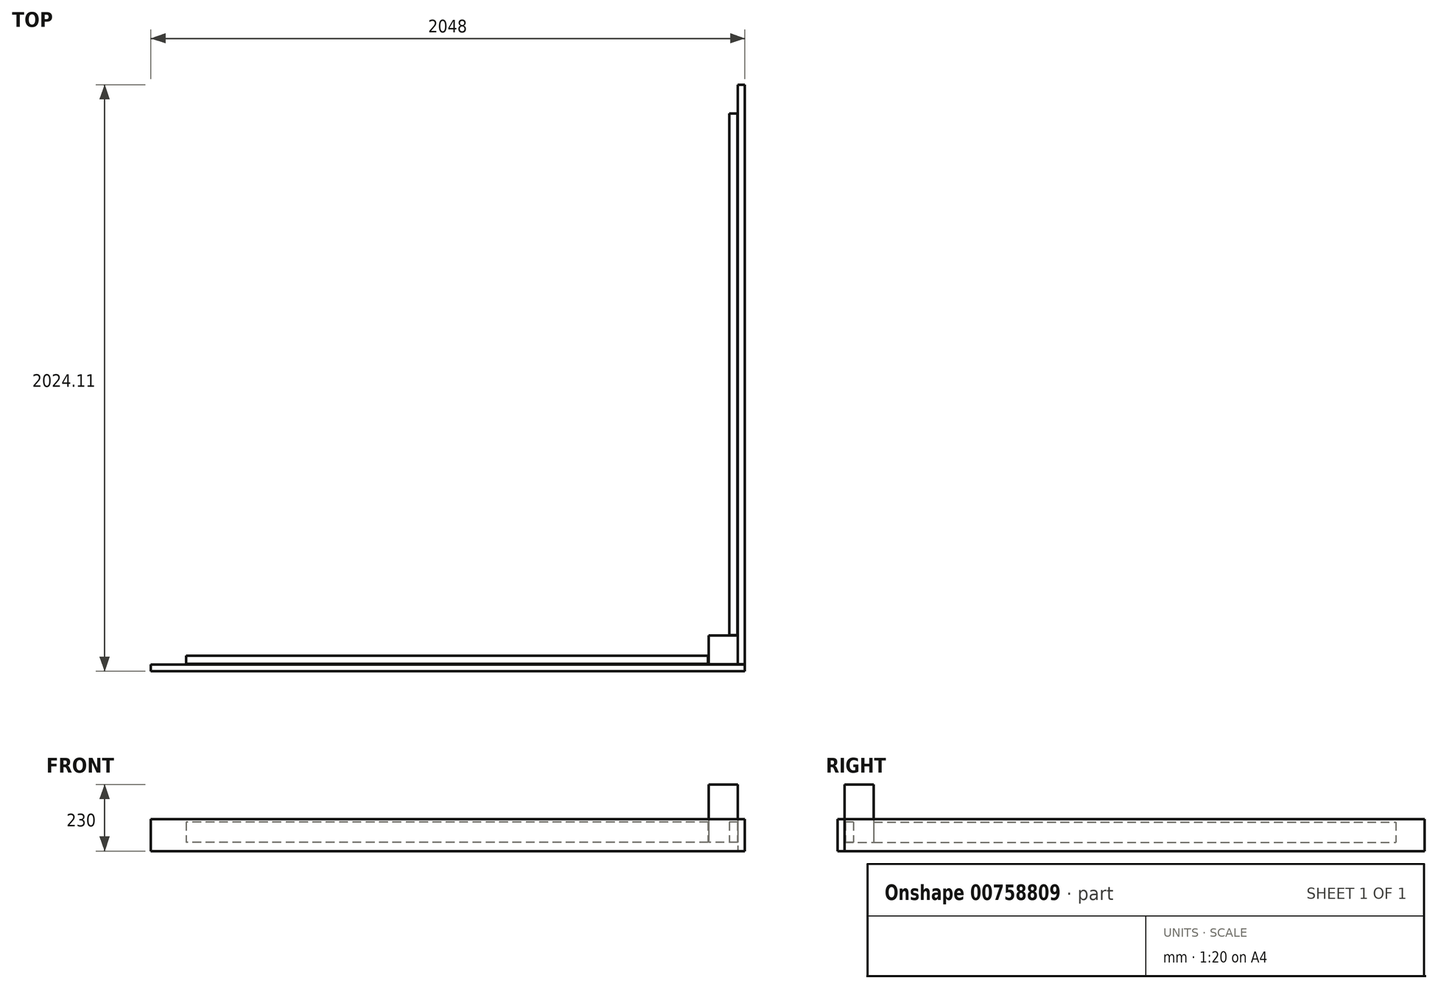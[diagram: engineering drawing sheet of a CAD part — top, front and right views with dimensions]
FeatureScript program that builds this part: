
annotation { "Feature Type Name" : "Feature", "Feature Type Description" : "" }
export const myFeature = defineFeature(function(context is Context, id is Id, definition is map)
    precondition{}
    {
        {
            var Q0;
            Q0=qCreatedBy(makeId("Top.planeOp"),FACE);
            var sketch = newSketch(context, id + "F0", { "sketchPlane" : qUnion([Q0])});
            skLineSegment(sketch, "E0.bottom", {"start": v(50, -50) * mm, "end": v(-50, -50) * mm});
            skLineSegment(sketch, "E0.top", {"start": v(50, 50) * mm, "end": v(-50, 50) * mm});
            skLineSegment(sketch, "E0.left", {"start": v(50, -50) * mm, "end": v(50, 50) * mm});
            skLineSegment(sketch, "E0.right", {"start": v(-50, -50) * mm, "end": v(-50, 50) * mm});
            skPoint(sketch, "E0.middle", {"position": v(0, 0) * mm});
            skSolve(sketch);
        }
        {
            var Q0;
            Q0 = qSketchRegion(id + "F0", true);
            extrude(context, id + "F1", {"entities" : qUnion([Q0]), "depth" : 200 * mm, "offsetDistance" : 25 * mm});
        }
        {
            var Q0;
            Q0=qCreatedBy(makeId("Top.planeOp"),FACE);
            var sketch = newSketch(context, id + "F2", { "sketchPlane" : qUnion([Q0])});
            skLineSegment(sketch, "E1.bottom", {"start": v(50.75, 1949.98) * mm, "end": v(74.75, 1949.98) * mm});
            skLineSegment(sketch, "E1.top", {"start": v(50.75, -50.02) * mm, "end": v(74.75, -50.02) * mm});
            skLineSegment(sketch, "E1.left", {"start": v(50.75, 1949.98) * mm, "end": v(50.75, -50.02) * mm});
            skLineSegment(sketch, "E1.right", {"start": v(74.75, 1949.98) * mm, "end": v(74.75, -50.02) * mm});
            skSolve(sketch);
        }
        {
            var Q0;
            Q0 = qSketchRegion(id + "F2", true);
            extrude(context, id + "F3", {"entities" : qUnion([Q0]), "depth" : 110 * mm, "offsetDistance" : 25 * mm});
        }
        {
            var Q0;
            Q0=makeQuery(id+"F3.opExtrude","SWEPT_BODY",BODY,{"disambiguationData":[OSD([sQuery(id+"F2.wireOp",EDGE,"E1.bottom"),sQuery(id+"F2.wireOp",EDGE,"E1.top"),sQuery(id+"F2.wireOp",EDGE,"E1.left"),sQuery(id+"F2.wireOp",EDGE,"E1.right")])]});
            transform(context, id + "F4", {"entities" : qUnion([Q0]), "transformType" : TransformType.TRANSLATION_3D, "dx" : 0 * mm, "dy" : 0 * mm, "dz" : -30 * mm, "makeCopy" : false});
        }
        {
            var Q0;
            Q0=qCreatedBy(makeId("Top.planeOp"),FACE);
            var sketch = newSketch(context, id + "F5", { "sketchPlane" : qUnion([Q0])});
            skLineSegment(sketch, "E2.bottom", {"start": v(49.68, 50.74) * mm, "end": v(21.68, 50.74) * mm});
            skLineSegment(sketch, "E2.top", {"start": v(49.68, 1850.74) * mm, "end": v(21.68, 1850.74) * mm});
            skLineSegment(sketch, "E2.left", {"start": v(49.68, 50.74) * mm, "end": v(49.68, 1850.74) * mm});
            skLineSegment(sketch, "E2.right", {"start": v(21.68, 50.74) * mm, "end": v(21.68, 1850.74) * mm});
            skSolve(sketch);
        }
        {
            var Q0;
            Q0 = qSketchRegion(id + "F5", true);
            extrude(context, id + "F6", {"entities" : qUnion([Q0]), "depth" : 70 * mm, "offsetDistance" : 25 * mm});
        }
        {
            var Q0;
            Q0=qCreatedBy(makeId("Top.planeOp"),FACE);
            var sketch = newSketch(context, id + "F7", { "sketchPlane" : qUnion([Q0])});
            skLineSegment(sketch, "E3.bottom", {"start": v(74.76, -50.13) * mm, "end": v(-1973.24, -50.13) * mm});
            skLineSegment(sketch, "E3.top", {"start": v(74.76, -74.13) * mm, "end": v(-1973.24, -74.13) * mm});
            skLineSegment(sketch, "E3.left", {"start": v(74.76, -50.13) * mm, "end": v(74.76, -74.13) * mm});
            skLineSegment(sketch, "E3.right", {"start": v(-1973.24, -50.13) * mm, "end": v(-1973.24, -74.13) * mm});
            skSolve(sketch);
        }
        {
            var Q0;
            Q0 = qSketchRegion(id + "F7", true);
            extrude(context, id + "F8", {"entities" : qUnion([Q0]), "depth" : 110 * mm, "offsetDistance" : 25 * mm});
        }
        {
            var Q0;
            Q0=makeQuery(id+"F8.opExtrude","SWEPT_BODY",BODY,{"disambiguationData":[OSD([sQuery(id+"F7.wireOp",EDGE,"E3.bottom"),sQuery(id+"F7.wireOp",EDGE,"E3.top"),sQuery(id+"F7.wireOp",EDGE,"E3.left"),sQuery(id+"F7.wireOp",EDGE,"E3.right")])]});
            transform(context, id + "F9", {"entities" : qUnion([Q0]), "transformType" : TransformType.TRANSLATION_3D, "dx" : 0 * mm, "dy" : 0 * mm, "dz" : -30 * mm, "makeCopy" : false});
        }
        {
            var Q0;
            Q0=qCreatedBy(makeId("Top.planeOp"),FACE);
            var sketch = newSketch(context, id + "F10", { "sketchPlane" : qUnion([Q0])});
            skLineSegment(sketch, "E4.bottom", {"start": v(-52.17, -19.74) * mm, "end": v(-1852.17, -19.74) * mm});
            skLineSegment(sketch, "E4.top", {"start": v(-52.17, -47.74) * mm, "end": v(-1852.17, -47.74) * mm});
            skLineSegment(sketch, "E4.left", {"start": v(-52.17, -19.74) * mm, "end": v(-52.17, -47.74) * mm});
            skLineSegment(sketch, "E4.right", {"start": v(-1852.17, -19.74) * mm, "end": v(-1852.17, -47.74) * mm});
            skSolve(sketch);
        }
        {
            var Q0;
            Q0 = qSketchRegion(id + "F10", true);
            extrude(context, id + "F11", {"entities" : qUnion([Q0]), "operationType" : NewBodyOperationType.ADD, "depth" : 70 * mm, "offsetDistance" : 25 * mm});
        }
    });
